# Revit family: RRFRALUSLTO
name_source: partatom
category: Generic Models
revit_build: Autodesk Revit 2018 (Build: 20190510_1515(x64)
units: mm (PartAtom-declared; Revit-internal decimal feet)

## family parameters
Always vertical = No
Can host rebar = No
Cut with Voids When Loaded = No
Part Type = Normal
Room Calculation Point = No
Round Connector Dimension = Use Diameter
Shared = Yes
Work Plane-Based = Yes

## types (6) — shared parameters
Default Elevation = 48 "
Patent Information = D649,863

## per-type parameters (varying)
| type | 1 Slot | 2 Slots | Description | Left Slot Length | Left Slot Length 2 | Rack Length | Right Slot Length | Right Slot Offset |
| RRFRALU36SLTO | No | Yes | Flat Rack ALU 36 Inch long Slot Only | 16.5 " | 16.5 " | 36 " | 16.5 " | 18.5 " |
| RRFRALU12SLTO | Yes | No | Flat Rack ALU 12 Inch long Slot Only | 10 " | 1 " | 12 " | 1 " | 4 " |
| RRFRALU18SLTO | Yes | No | Flat Rack ALU 18 Inch long Slot Only | 16 " | 1 " | 18 " | 1 " | 4 " |
| RRFRALU24SLTO | Yes | No | Flat Rack ALU 24 Inch long Slot Only | 22 " | 1 " | 24 " | 1 " | 4 " |
| RRFRALU30SLTO | Yes | No | Flat Rack ALU 30 Inch long Slot Only | 28 " | 1 " | 30 " | 1 " | 4 " |
| RRFRALU48SLTO | No | Yes | Flat Rack ALU 48 Inch long Slot Only | 22.5 " | 22.5 " | 48 " | 22.5 " | 24.5 " |

note: column(s) folded — value = type name in every type: Catalog Number

## geometry (parser evidence)
native form markers: Sweep x3
no freeform markers — native parametric forms only
